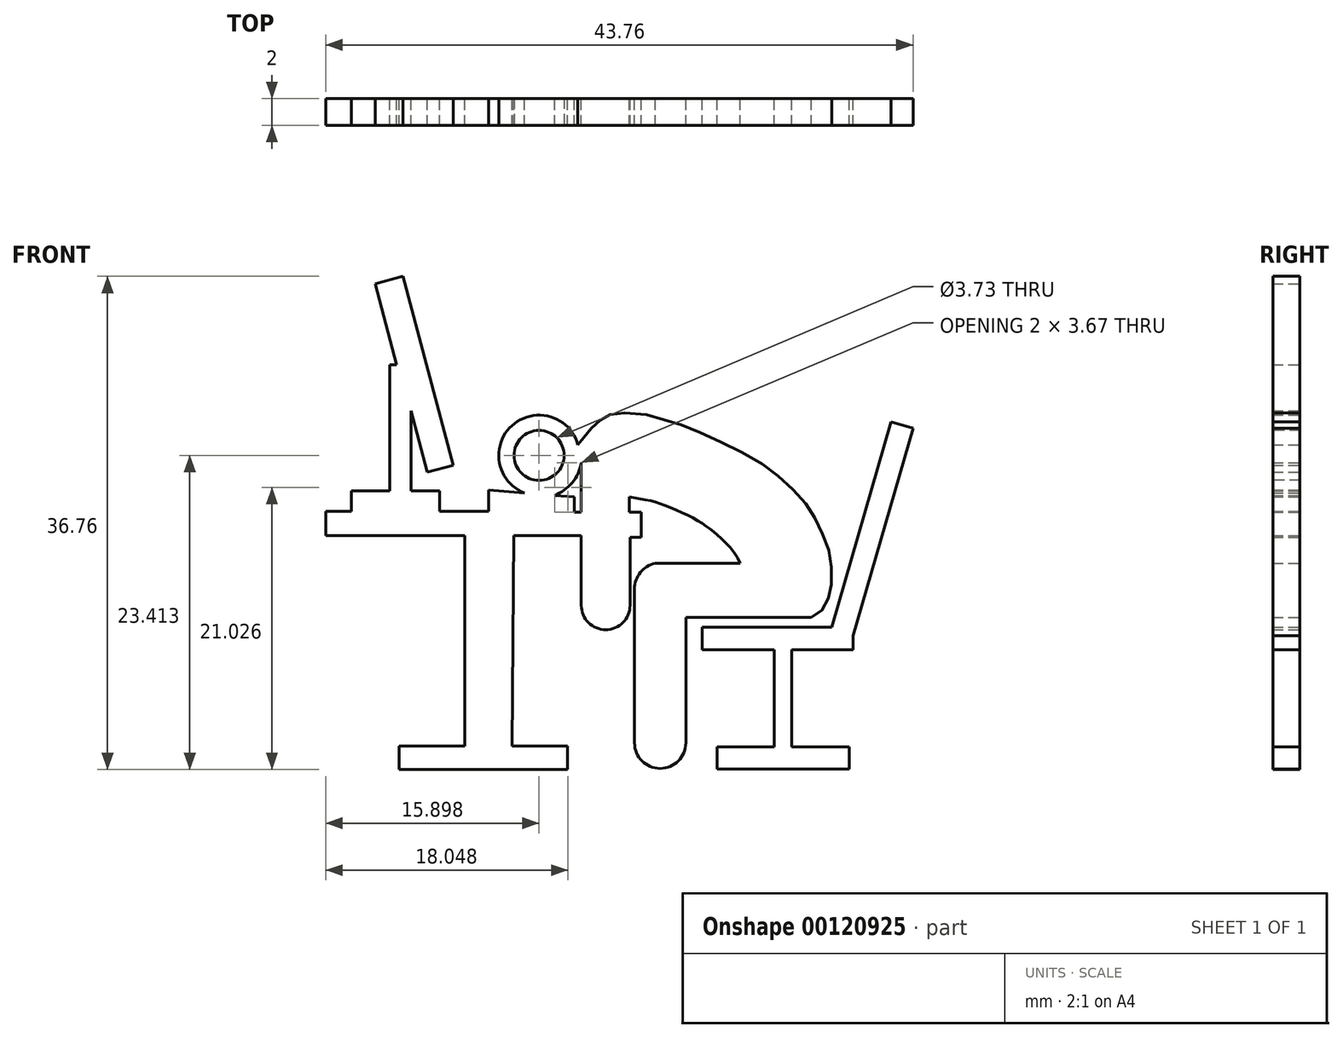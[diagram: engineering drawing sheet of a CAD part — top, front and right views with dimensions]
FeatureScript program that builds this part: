
annotation { "Feature Type Name" : "Feature", "Feature Type Description" : "" }
export const myFeature = defineFeature(function(context is Context, id is Id, definition is map)
    precondition{}
    {
        {
            var Q0;
            Q0=qCreatedBy(makeId("Front.planeOp"),FACE);
            var sketch = newSketch(context, id + "F0", { "sketchPlane" : qUnion([Q0])});
            skFitSpline(sketch, "E0", {"points": [v(18.92, 19.99) * mm, v(21.2, 19.49) * mm, v(23.19, 18.66) * mm, v(24.69, 17.78) * mm, v(25.8, 16.85) * mm, v(27.18, 15.04) * mm], "startDerivative": vector(18.15, -3.1) * mm, "endDerivative": vector(2.57, -8.85) * mm});
            skLineSegment(sketch, "E1", {"start": v(18.92, 19.99) * mm, "end": v(18.92, 18.83) * mm});
            skLineSegment(sketch, "E2", {"start": v(18.92, 18.83) * mm, "end": v(19.81, 18.83) * mm});
            skLineSegment(sketch, "E3", {"start": v(19.81, 18.83) * mm, "end": v(19.81, 16.97) * mm});
            skLineSegment(sketch, "E4", {"start": v(19.81, 16.97) * mm, "end": v(18.99, 16.97) * mm});
            skLineSegment(sketch, "E5", {"start": v(15.36, 22.52) * mm, "end": v(15.36, 18.85) * mm});
            skLineSegment(sketch, "E6", {"start": v(18.99, 16.97) * mm, "end": v(18.99, 11.9) * mm});
            skLineSegment(sketch, "E7", {"start": v(2.07, 36.42) * mm, "end": v(0, 35.87) * mm});
            skLineSegment(sketch, "E8", {"start": v(0, 35.87) * mm, "end": v(1.6, 29.82) * mm});
            skLineSegment(sketch, "E9", {"start": v(1.6, 29.82) * mm, "end": v(1.09, 29.82) * mm});
            skLineSegment(sketch, "E10", {"start": v(2.07, 36.42) * mm, "end": v(5.82, 22.33) * mm});
            skLineSegment(sketch, "E11", {"start": v(5.82, 22.33) * mm, "end": v(3.89, 21.82) * mm});
            skLineSegment(sketch, "E12", {"start": v(3.89, 21.82) * mm, "end": v(2.68, 26.39) * mm});
            skLineSegment(sketch, "E13", {"start": v(1.09, 29.82) * mm, "end": v(1.09, 20.43) * mm});
            skLineSegment(sketch, "E14", {"start": v(1.09, 20.43) * mm, "end": v(-1.79, 20.43) * mm});
            skLineSegment(sketch, "E15", {"start": v(-1.79, 20.43) * mm, "end": v(-1.79, 18.9) * mm});
            skLineSegment(sketch, "E16", {"start": v(-1.79, 18.9) * mm, "end": v(-3.69, 18.9) * mm});
            skLineSegment(sketch, "E17", {"start": v(-3.69, 18.9) * mm, "end": v(-3.69, 17.1) * mm});
            skLineSegment(sketch, "E18", {"start": v(-3.69, 17.1) * mm, "end": v(6.67, 17.1) * mm});
            skLineSegment(sketch, "E19", {"start": v(2.68, 26.39) * mm, "end": v(2.68, 20.43) * mm});
            skLineSegment(sketch, "E20", {"start": v(2.68, 20.43) * mm, "end": v(4.8, 20.43) * mm});
            skLineSegment(sketch, "E21", {"start": v(4.8, 20.43) * mm, "end": v(4.8, 18.9) * mm});
            skLineSegment(sketch, "E22", {"start": v(4.8, 18.9) * mm, "end": v(8.45, 18.9) * mm});
            skLineSegment(sketch, "E23", {"start": v(8.45, 18.9) * mm, "end": v(8.45, 20.5) * mm});
            skLineSegment(sketch, "E24", {"start": v(8.45, 20.5) * mm, "end": v(11.13, 20.27) * mm});
            skLineSegment(sketch, "E25.trimOffspring", {"start": v(13.36, 20.1) * mm, "end": v(14.85, 19.97) * mm});
            skArc(sketch, "E26.trimOffspring", {"start": v(15.1, 23.86) * mm, "mid": v(10.2, 25.3) * mm, "end": v(11.13, 20.27) * mm});
            skArc(sketch, "E27", {"start": v(13.36, 20.1) * mm, "mid": v(14.68, 21.04) * mm, "end": v(15.36, 22.52) * mm});
            skLineSegment(sketch, "E28", {"start": v(14.85, 19.97) * mm, "end": v(14.85, 18.85) * mm});
            skLineSegment(sketch, "E29", {"start": v(14.85, 18.85) * mm, "end": v(15.36, 18.85) * mm});
            skLineSegment(sketch, "E30", {"start": v(10.32, 17.1) * mm, "end": v(15.36, 17.1) * mm});
            skLineSegment(sketch, "E31.trimOffspring", {"start": v(15.36, 17.1) * mm, "end": v(15.36, 11.9) * mm});
            skLineSegment(sketch, "E32", {"start": v(15.36, 11.9) * mm, "end": v(18.99, 11.9) * mm, "construction": true});
            skArc(sketch, "E33", {"start": v(15.36, 11.9) * mm, "mid": v(17.17, 10.08) * mm, "end": v(18.99, 11.9) * mm});
            skLineSegment(sketch, "E34", {"start": v(6.67, 17.1) * mm, "end": v(6.67, 1.4) * mm});
            skLineSegment(sketch, "E35", {"start": v(6.67, 1.4) * mm, "end": v(1.8, 1.4) * mm});
            skLineSegment(sketch, "E36", {"start": v(1.8, 1.4) * mm, "end": v(1.8, -0.34) * mm});
            skLineSegment(sketch, "E37", {"start": v(1.8, -0.34) * mm, "end": v(14.33, -0.34) * mm});
            skLineSegment(sketch, "E38", {"start": v(14.33, -0.34) * mm, "end": v(14.33, 1.4) * mm});
            skLineSegment(sketch, "E39", {"start": v(14.33, 1.4) * mm, "end": v(10.2, 1.4) * mm});
            skLineSegment(sketch, "E40", {"start": v(10.2, 1.4) * mm, "end": v(10.32, 17.1) * mm});
            skLineSegment(sketch, "E41", {"start": v(27.18, 15.04) * mm, "end": v(20.87, 15.04) * mm});
            skLineSegment(sketch, "E42", {"start": v(19.32, 13.11) * mm, "end": v(19.32, 1.65) * mm});
            skArc(sketch, "E43", {"start": v(20.87, 15.04) * mm, "mid": v(19.75, 14.35) * mm, "end": v(19.32, 13.11) * mm});
            skLineSegment(sketch, "E44", {"start": v(23.14, 11) * mm, "end": v(23.14, 1.65) * mm});
            skLineSegment(sketch, "E45", {"start": v(19.32, 1.65) * mm, "end": v(23.14, 1.65) * mm, "construction": true});
            skArc(sketch, "E46", {"start": v(19.32, 1.65) * mm, "mid": v(21.23, -0.26) * mm, "end": v(23.14, 1.65) * mm});
            skLineSegment(sketch, "E47", {"start": v(23.14, 11) * mm, "end": v(32.48, 11) * mm});
            skFitSpline(sketch, "E48", {"points": [v(32.48, 11) * mm, v(33.15, 11.43) * mm, v(33.6, 11.98) * mm, v(33.88, 12.91) * mm, v(34.02, 13.71) * mm, v(33.95, 15.2) * mm, v(33.67, 16.38) * mm, v(33.08, 17.72) * mm, v(32.48, 18.87) * mm, v(31.67, 19.95) * mm, v(30.4, 21.2) * mm, v(29.05, 22.26) * mm, v(27.02, 23.44) * mm, v(24.78, 24.52) * mm, v(22.98, 25.28) * mm, v(21.58, 25.71) * mm, v(20.13, 26.12) * mm, v(18.15, 26.24) * mm, v(17.43, 26.08) * mm, v(16.96, 25.83) * mm, v(16.52, 25.5) * mm, v(16.03, 25.02) * mm, v(15.61, 24.5) * mm, v(15.33, 24.14) * mm, v(15.1, 23.86) * mm], "startDerivative": vector(20.38, 11.93) * mm, "endDerivative": vector(-16.88, -20.57) * mm});
            skLineSegment(sketch, "E49", {"start": v(34, 10.28) * mm, "end": v(24.35, 10.28) * mm});
            skLineSegment(sketch, "E50", {"start": v(24.35, 10.28) * mm, "end": v(24.35, 8.58) * mm});
            skLineSegment(sketch, "E51", {"start": v(24.35, 8.58) * mm, "end": v(29.73, 8.58) * mm});
            skLineSegment(sketch, "E52", {"start": v(29.73, 8.58) * mm, "end": v(29.73, 1.34) * mm});
            skLineSegment(sketch, "E53", {"start": v(31.01, 8.58) * mm, "end": v(31.01, 1.34) * mm});
            skLineSegment(sketch, "E54", {"start": v(31.01, 8.58) * mm, "end": v(35.61, 8.58) * mm});
            skLineSegment(sketch, "E55", {"start": v(35.61, 8.58) * mm, "end": v(35.61, 9.64) * mm});
            skLineSegment(sketch, "E56", {"start": v(29.73, 1.34) * mm, "end": v(25.47, 1.34) * mm});
            skLineSegment(sketch, "E57", {"start": v(25.47, 1.34) * mm, "end": v(25.47, -0.3) * mm});
            skLineSegment(sketch, "E58", {"start": v(25.47, -0.3) * mm, "end": v(35.3, -0.3) * mm});
            skLineSegment(sketch, "E59", {"start": v(35.3, -0.3) * mm, "end": v(35.3, 1.34) * mm});
            skLineSegment(sketch, "E60", {"start": v(35.3, 1.34) * mm, "end": v(31.01, 1.34) * mm});
            skLineSegment(sketch, "E61", {"start": v(34, 10.28) * mm, "end": v(38.42, 25.57) * mm});
            skLineSegment(sketch, "E62", {"start": v(38.42, 25.57) * mm, "end": v(40.07, 25.1) * mm});
            skLineSegment(sketch, "E63", {"start": v(40.07, 25.1) * mm, "end": v(35.61, 9.64) * mm});
            skSolve(sketch);
        }
        {
            var Q0;
            Q0 = qSketchRegion(id + "F0", true);
            extrude(context, id + "F1", {"entities" : qUnion([Q0]), "depth" : 2 * mm});
        }
        {
            var Q0;
            Q0=makeQuery(id+"F1.opExtrude","CAP_FACE",FACE,{"disambiguationData":[OSD([sQuery(id+"F0.wireOp",EDGE,"E0"),sQuery(id+"F0.wireOp",EDGE,"E1"),sQuery(id+"F0.wireOp",EDGE,"E2"),sQuery(id+"F0.wireOp",EDGE,"E3"),sQuery(id+"F0.wireOp",EDGE,"E4"),sQuery(id+"F0.wireOp",EDGE,"E5"),sQuery(id+"F0.wireOp",EDGE,"E6"),sQuery(id+"F0.wireOp",EDGE,"E7"),sQuery(id+"F0.wireOp",EDGE,"E8"),sQuery(id+"F0.wireOp",EDGE,"E9"),sQuery(id+"F0.wireOp",EDGE,"E10"),sQuery(id+"F0.wireOp",EDGE,"E11"),sQuery(id+"F0.wireOp",EDGE,"E12"),sQuery(id+"F0.wireOp",EDGE,"E13"),sQuery(id+"F0.wireOp",EDGE,"E14"),sQuery(id+"F0.wireOp",EDGE,"E15"),sQuery(id+"F0.wireOp",EDGE,"E16"),sQuery(id+"F0.wireOp",EDGE,"E17"),sQuery(id+"F0.wireOp",EDGE,"E18"),sQuery(id+"F0.wireOp",EDGE,"E19"),sQuery(id+"F0.wireOp",EDGE,"E20"),sQuery(id+"F0.wireOp",EDGE,"E21"),sQuery(id+"F0.wireOp",EDGE,"E22"),sQuery(id+"F0.wireOp",EDGE,"E23"),sQuery(id+"F0.wireOp",EDGE,"E24"),sQuery(id+"F0.wireOp",EDGE,"E25.trimOffspring"),sQuery(id+"F0.wireOp",EDGE,"E26.trimOffspring"),sQuery(id+"F0.wireOp",EDGE,"E27"),sQuery(id+"F0.wireOp",EDGE,"E28"),sQuery(id+"F0.wireOp",EDGE,"E29"),sQuery(id+"F0.wireOp",EDGE,"E30"),sQuery(id+"F0.wireOp",EDGE,"E31.trimOffspring"),sQuery(id+"F0.wireOp",EDGE,"E33"),sQuery(id+"F0.wireOp",EDGE,"E34"),sQuery(id+"F0.wireOp",EDGE,"E35"),sQuery(id+"F0.wireOp",EDGE,"E36"),sQuery(id+"F0.wireOp",EDGE,"E37"),sQuery(id+"F0.wireOp",EDGE,"E38"),sQuery(id+"F0.wireOp",EDGE,"E39"),sQuery(id+"F0.wireOp",EDGE,"E40"),sQuery(id+"F0.wireOp",EDGE,"E41"),sQuery(id+"F0.wireOp",EDGE,"E42"),sQuery(id+"F0.wireOp",EDGE,"E43"),sQuery(id+"F0.wireOp",EDGE,"E44"),sQuery(id+"F0.wireOp",EDGE,"E46"),sQuery(id+"F0.wireOp",EDGE,"E47"),sQuery(id+"F0.wireOp",EDGE,"E48")])],"isStart":false});
            var sketch = newSketch(context, id + "F2", { "sketchPlane" : qUnion([Q0])});
            skCircle(sketch, "E64", {"center": v(12.2, 23.07) * mm, "radius": 1.86 * mm});
            skSolve(sketch);
        }
        {
            var Q0;
            Q0 = qSketchRegion(id + "F2", true);
            extrude(context, id + "F3", {"entities" : qUnion([Q0]), "operationType" : NewBodyOperationType.REMOVE, "oppositeDirection" : true, "depth" : 25 * mm});
        }
    });
